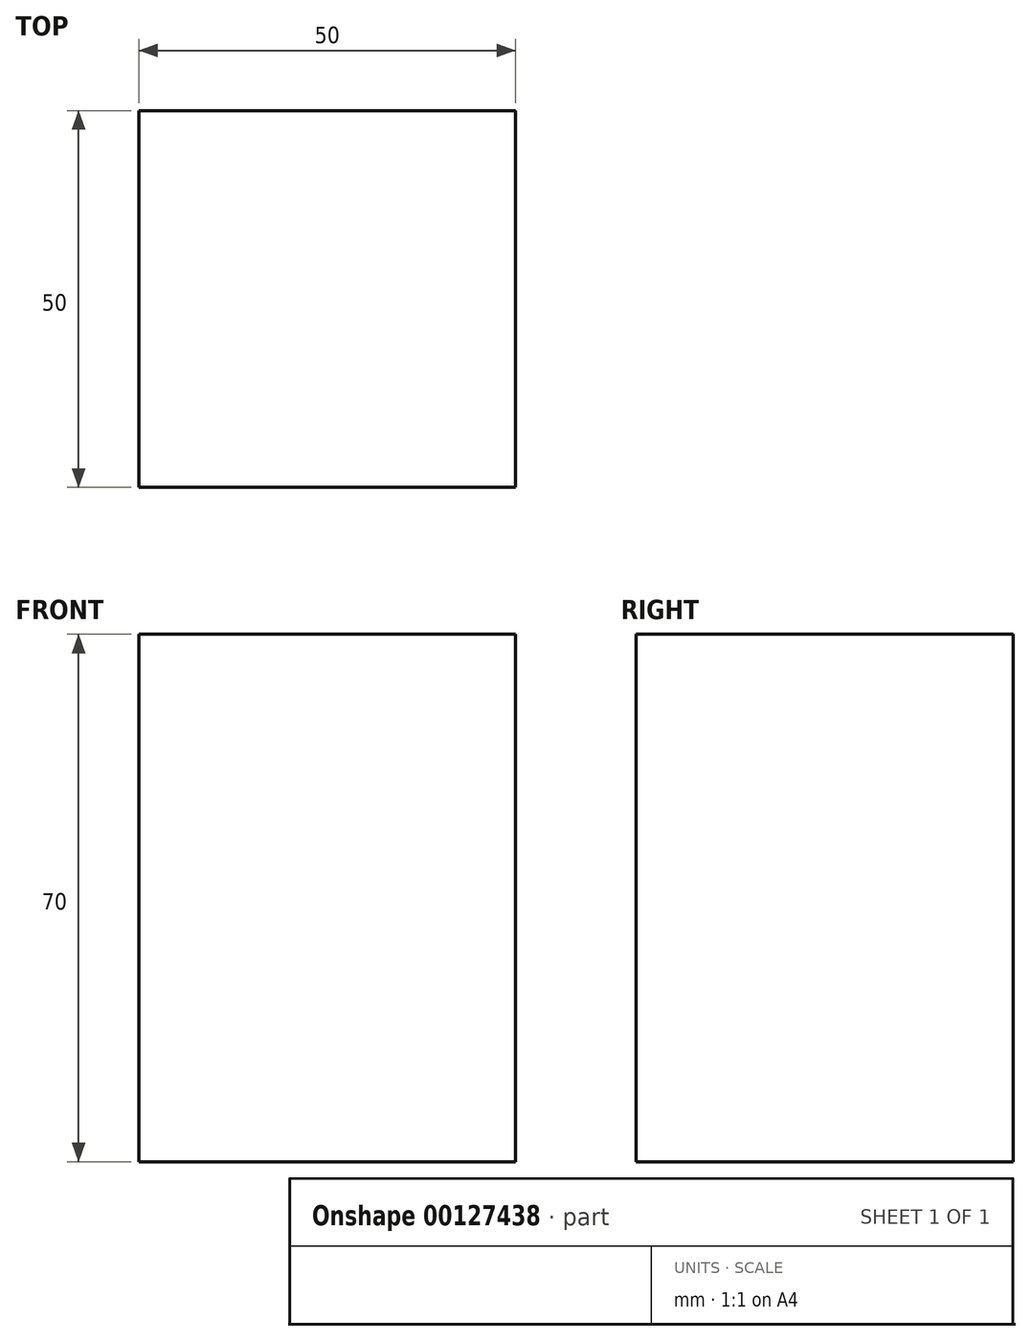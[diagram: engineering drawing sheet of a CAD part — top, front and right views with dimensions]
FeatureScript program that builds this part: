
annotation { "Feature Type Name" : "Feature", "Feature Type Description" : "" }
export const myFeature = defineFeature(function(context is Context, id is Id, definition is map)
    precondition{}
    {
        {
            var Q0;
            Q0=qCreatedBy(makeId("Top.planeOp"),FACE);
            var sketch = newSketch(context, id + "F0", { "sketchPlane" : qUnion([Q0])});
            skLineSegment(sketch, "E0.bottom", {"start": v(-25, 25) * mm, "end": v(25, 25) * mm});
            skLineSegment(sketch, "E0.top", {"start": v(-25, -25) * mm, "end": v(25, -25) * mm});
            skLineSegment(sketch, "E0.left", {"start": v(-25, 25) * mm, "end": v(-25, -25) * mm});
            skLineSegment(sketch, "E0.right", {"start": v(25, 25) * mm, "end": v(25, -25) * mm});
            skPoint(sketch, "E0.middle", {"position": v(0, 0) * mm});
            skSolve(sketch);
        }
        {
            var Q0;
            Q0=makeQuery(id+"F0.imprint","IMPRINT",FACE,{"disambiguationData":[TD([[makeQuery(id+"F0.imprint","IMPRINT",EDGE,{"derivedFrom":sQuery(id+"F0.wireOp",EDGE,"E0.bottom")}),-1.0]])]});
            extrude(context, id + "F1", {"entities" : qUnion([Q0]), "depth" : 70 * mm});
        }
    });
